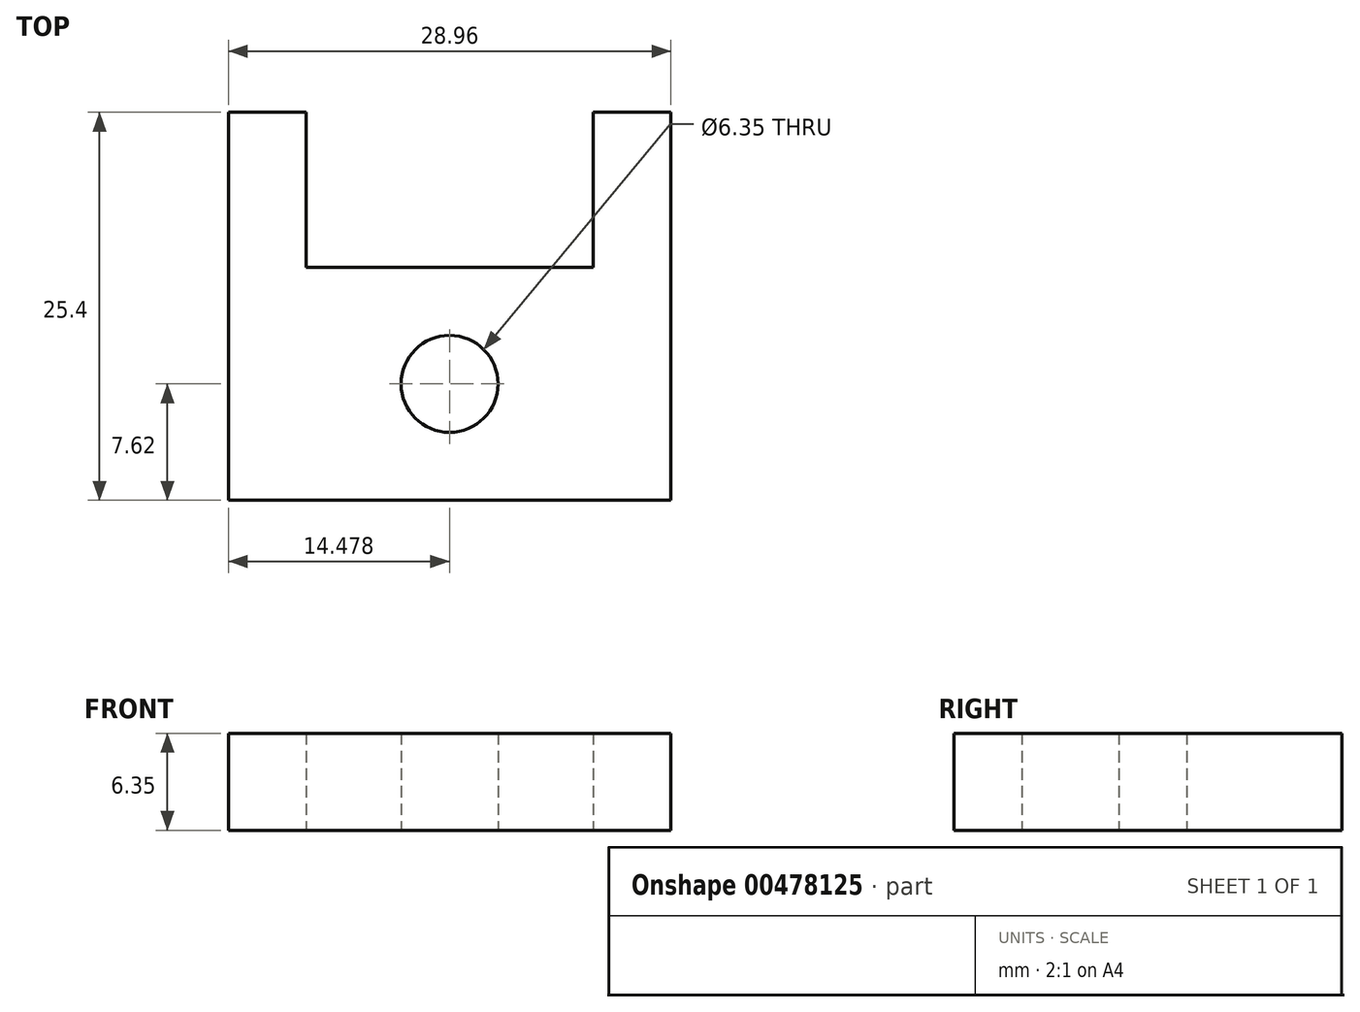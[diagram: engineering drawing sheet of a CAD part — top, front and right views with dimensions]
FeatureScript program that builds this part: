
annotation { "Feature Type Name" : "Feature", "Feature Type Description" : "" }
export const myFeature = defineFeature(function(context is Context, id is Id, definition is map)
    precondition{}
    {
        {
            var Q0;
            Q0=qCreatedBy(makeId("Top.planeOp"),FACE);
            var sketch = newSketch(context, id + "F0", { "sketchPlane" : qUnion([Q0])});
            skLineSegment(sketch, "E0", {"start": v(0, 0) * mm, "end": v(0, 25.4) * mm});
            skLineSegment(sketch, "E1", {"start": v(0, 25.4) * mm, "end": v(5.08, 25.4) * mm});
            skLineSegment(sketch, "E2", {"start": v(5.08, 25.4) * mm, "end": v(5.08, 15.24) * mm});
            skLineSegment(sketch, "E3", {"start": v(0, 0) * mm, "end": v(28.96, 0) * mm});
            skLineSegment(sketch, "E4", {"start": v(28.96, 0) * mm, "end": v(28.96, 25.4) * mm});
            skLineSegment(sketch, "E5", {"start": v(28.96, 25.4) * mm, "end": v(23.88, 25.4) * mm});
            skLineSegment(sketch, "E6", {"start": v(23.88, 25.4) * mm, "end": v(23.88, 15.24) * mm});
            skLineSegment(sketch, "E7", {"start": v(23.88, 15.24) * mm, "end": v(5.08, 15.24) * mm});
            skLineSegment(sketch, "E8", {"start": v(0, 0) * mm, "end": v(14.48, 0) * mm});
            skPoint(sketch, "E9.endSnap0", {"position": v(14.48, 15.24) * mm});
            skCircle(sketch, "E10", {"center": v(14.48, 7.62) * mm, "radius": 3.18 * mm});
            skSolve(sketch);
        }
        {
            var Q0;
            Q0=makeQuery(id+"F0.imprint","IMPRINT",FACE,{"disambiguationData":[TD([[makeQuery(id+"F0.imprint","IMPRINT",EDGE,{"derivedFrom":sQuery(id+"F0.wireOp",EDGE,"E0")}),-1.0]])]});
            extrude(context, id + "F1", {"entities" : qUnion([Q0]), "depth" : 6.35 * mm, "offsetDistance" : 25.4 * mm});
        }
    });
